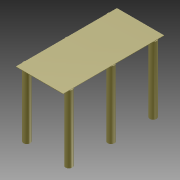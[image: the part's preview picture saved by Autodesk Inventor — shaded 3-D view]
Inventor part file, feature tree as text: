
AUTODESK INVENTOR PART (.ipt)
format: ipt  version: 2011 SP1 (Build 150282100, 282)  size: 93,696 bytes
history: native  units: in
note: dims shown in document units (in); Inventor stores cm internally (conversion verified against a paired STEP export)
features: other x7, extrude x2, sketch x2, pattern_linear x1
ambient origin geometry x8: Origin, YZ Plane, XZ Plane, XY Plane, X Axis, Y Axis, Z Axis, Center Point
bodies: Solid1 (feature_tree)
feature tree (12):
  extrude  "Extrusion1"  Depth=0.16in TaperAngle=0.0deg
  extrude  "Extrusion2"  [1 undecoded]
  pattern_linear  "Rectangular Pattern1"  [2 undecoded]
  other  "to_body_XY"
  other  "to_body_YZ"
  other  "to_body_ZX"
  other  "to_body_X"
  other  "to_body_Y"
  other  "to_body_Z"
  other  "to_body_Center"
  sketch  "Sketch_1"  dims[d0=0.001in d1=0.0in d2=0.16in d3=0.0in]
  sketch  "Sketch_2"  dims[d4=0.7874in d6=0.1in d7=1.1811in d9=0.1in]
note: 3 required parameter values undecoded (feature->parameter linkage not recoverable at this tier; creation-order binding heuristic only, values carry confidence <= 0.55)
